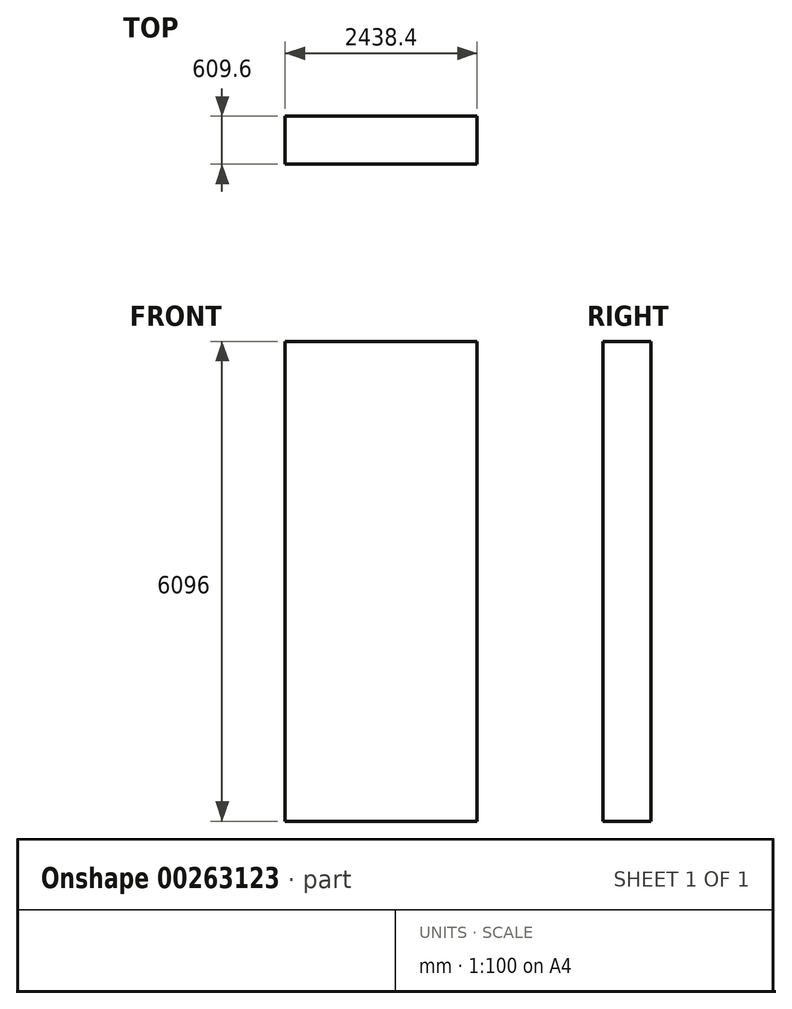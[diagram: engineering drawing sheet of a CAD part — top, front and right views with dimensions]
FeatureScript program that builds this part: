
annotation { "Feature Type Name" : "Feature", "Feature Type Description" : "" }
export const myFeature = defineFeature(function(context is Context, id is Id, definition is map)
    precondition{}
    {
        {
            var Q0;
            Q0=qCreatedBy(makeId("Top.planeOp"),FACE);
            var sketch = newSketch(context, id + "F0", { "sketchPlane" : qUnion([Q0])});
            skLineSegment(sketch, "E0.bottom", {"start": v(-1219.2, 304.8) * mm, "end": v(1219.2, 304.8) * mm});
            skLineSegment(sketch, "E0.top", {"start": v(-1219.2, -304.8) * mm, "end": v(1219.2, -304.8) * mm});
            skLineSegment(sketch, "E0.left", {"start": v(-1219.2, 304.8) * mm, "end": v(-1219.2, -304.8) * mm});
            skLineSegment(sketch, "E0.right", {"start": v(1219.2, 304.8) * mm, "end": v(1219.2, -304.8) * mm});
            skPoint(sketch, "E0.middle", {"position": v(0, 0) * mm});
            skSolve(sketch);
        }
        {
            var Q0;
            Q0 = qSketchRegion(id + "F0", true);
            extrude(context, id + "F1", {"entities" : qUnion([Q0]), "depth" : 6096 * mm});
        }
    });
